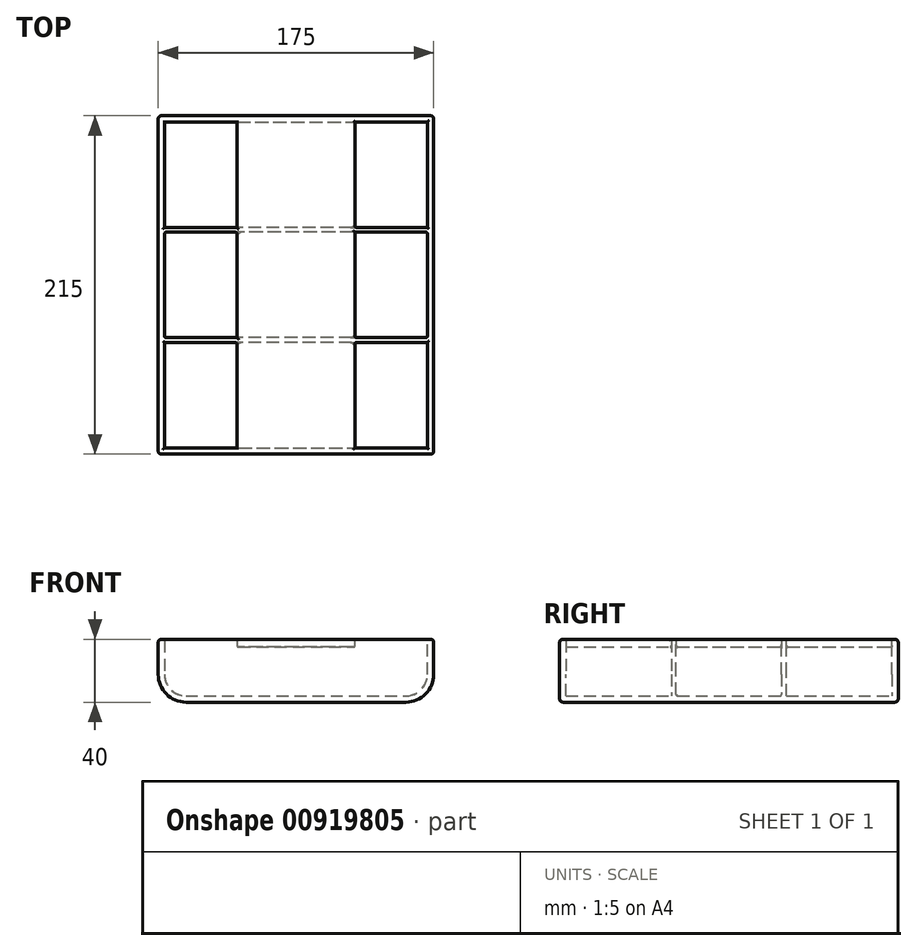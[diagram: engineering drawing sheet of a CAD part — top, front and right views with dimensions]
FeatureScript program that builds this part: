
annotation { "Feature Type Name" : "Feature", "Feature Type Description" : "" }
export const myFeature = defineFeature(function(context is Context, id is Id, definition is map)
    precondition{}
    {
        {
            var Q0;
            Q0=qCreatedBy(makeId("Front.planeOp"),FACE);
            var sketch = newSketch(context, id + "F0", { "sketchPlane" : qUnion([Q0])});
            skLineSegment(sketch, "E0", {"start": v(-91.07, 3.96) * mm, "end": v(-87.07, 3.96) * mm});
            skLineSegment(sketch, "E1", {"start": v(-87.07, 3.96) * mm, "end": v(-87.07, -18.39) * mm});
            skLineSegment(sketch, "E2", {"start": v(-73.42, -32.04) * mm, "end": v(66.28, -32.04) * mm});
            skLineSegment(sketch, "E3", {"start": v(79.93, -18.39) * mm, "end": v(79.93, 3.96) * mm});
            skLineSegment(sketch, "E4", {"start": v(79.93, 3.96) * mm, "end": v(83.93, 3.96) * mm});
            skLineSegment(sketch, "E5", {"start": v(83.93, 3.96) * mm, "end": v(83.93, -18.39) * mm});
            skLineSegment(sketch, "E6", {"start": v(66.28, -36.04) * mm, "end": v(-73.42, -36.04) * mm});
            skLineSegment(sketch, "E7", {"start": v(-91.07, -18.39) * mm, "end": v(-91.07, 3.96) * mm});
            skArc(sketch, "E8", {"start": v(-91.07, -18.39) * mm, "mid": v(-85.9, -30.87) * mm, "end": v(-73.42, -36.04) * mm});
            skArc(sketch, "E9", {"start": v(-87.07, -18.39) * mm, "mid": v(-83.07, -28.04) * mm, "end": v(-73.42, -32.04) * mm});
            skArc(sketch, "E10", {"start": v(66.28, -32.04) * mm, "mid": v(75.93, -28.04) * mm, "end": v(79.93, -18.39) * mm});
            skArc(sketch, "E11", {"start": v(66.28, -36.04) * mm, "mid": v(78.76, -30.87) * mm, "end": v(83.93, -18.39) * mm});
            skSolve(sketch);
        }
        {
            var Q0;
            Q0 = qSketchRegion(id + "F0", true);
            extrude(context, id + "F1", {"entities" : qUnion([Q0]), "depth" : (67 * 3 + 6) * mm, "offsetDistance" : 25 * mm});
        }
        {
            var Q0;
            Q0=makeQuery(id+"F1.opExtrude","CAP_FACE",FACE,{"disambiguationData":[OSD([sQuery(id+"F0.wireOp",EDGE,"E0"),sQuery(id+"F0.wireOp",EDGE,"E1"),sQuery(id+"F0.wireOp",EDGE,"E2"),sQuery(id+"F0.wireOp",EDGE,"E3"),sQuery(id+"F0.wireOp",EDGE,"E4"),sQuery(id+"F0.wireOp",EDGE,"E5"),sQuery(id+"F0.wireOp",EDGE,"E6"),sQuery(id+"F0.wireOp",EDGE,"E7"),sQuery(id+"F0.wireOp",EDGE,"E8"),sQuery(id+"F0.wireOp",EDGE,"E9"),sQuery(id+"F0.wireOp",EDGE,"E10"),sQuery(id+"F0.wireOp",EDGE,"E11")])],"isStart":false});
            var sketch = newSketch(context, id + "F2", { "sketchPlane" : qUnion([Q0])});
            skLineSegment(sketch, "E12", {"start": v(-91.07, 3.96) * mm, "end": v(-91.07, -18.39) * mm});
            skLineSegment(sketch, "E13", {"start": v(-91.07, 3.96) * mm, "end": v(83.93, 3.96) * mm});
            skLineSegment(sketch, "E14", {"start": v(83.93, 3.96) * mm, "end": v(83.93, -18.39) * mm});
            skLineSegment(sketch, "E15", {"start": v(66.28, -36.04) * mm, "end": v(-73.42, -36.04) * mm});
            skArc(sketch, "E16", {"start": v(-91.07, -18.39) * mm, "mid": v(-85.9, -30.87) * mm, "end": v(-73.42, -36.04) * mm});
            skArc(sketch, "E17", {"start": v(66.28, -36.04) * mm, "mid": v(78.76, -30.87) * mm, "end": v(83.93, -18.39) * mm});
            skSolve(sketch);
        }
        {
            var Q0;
            Q0 = qSketchRegion(id + "F2", true);
            extrude(context, id + "F3", {"entities" : qUnion([Q0]), "operationType" : NewBodyOperationType.ADD, "depth" : 4 * mm, "offsetDistance" : 25 * mm});
        }
        {
            var Q0;
            Q0=makeQuery(id+"F1.opExtrude","CAP_FACE",FACE,{"disambiguationData":[OSD([sQuery(id+"F0.wireOp",EDGE,"E0"),sQuery(id+"F0.wireOp",EDGE,"E1"),sQuery(id+"F0.wireOp",EDGE,"E2"),sQuery(id+"F0.wireOp",EDGE,"E3"),sQuery(id+"F0.wireOp",EDGE,"E4"),sQuery(id+"F0.wireOp",EDGE,"E5"),sQuery(id+"F0.wireOp",EDGE,"E6"),sQuery(id+"F0.wireOp",EDGE,"E7"),sQuery(id+"F0.wireOp",EDGE,"E8"),sQuery(id+"F0.wireOp",EDGE,"E9"),sQuery(id+"F0.wireOp",EDGE,"E10"),sQuery(id+"F0.wireOp",EDGE,"E11")])],"isStart":true});
            var sketch = newSketch(context, id + "F4", { "sketchPlane" : qUnion([Q0])});
            skLineSegment(sketch, "E18", {"start": v(-83.93, -18.39) * mm, "end": v(-83.93, 3.96) * mm});
            skLineSegment(sketch, "E19", {"start": v(-83.93, 3.96) * mm, "end": v(91.07, 3.96) * mm});
            skLineSegment(sketch, "E20", {"start": v(91.07, 3.96) * mm, "end": v(91.07, -18.39) * mm});
            skLineSegment(sketch, "E21", {"start": v(73.42, -36.04) * mm, "end": v(-66.28, -36.04) * mm});
            skArc(sketch, "E22", {"start": v(-83.93, -18.39) * mm, "mid": v(-78.76, -30.87) * mm, "end": v(-66.28, -36.04) * mm});
            skArc(sketch, "E23", {"start": v(73.42, -36.04) * mm, "mid": v(85.9, -30.87) * mm, "end": v(91.07, -18.39) * mm});
            skSolve(sketch);
        }
        {
            var Q0;
            Q0 = qSketchRegion(id + "F4", true);
            extrude(context, id + "F5", {"entities" : qUnion([Q0]), "operationType" : NewBodyOperationType.ADD, "depth" : 4 * mm, "offsetDistance" : 25 * mm});
        }
        {
            var Q0;
            Q0=qCreatedBy(makeId("Front.planeOp"),FACE);
            cPlane(context, id + "F6", {"entities" : qUnion([Q0]), "cplaneType" : CPlaneType.OFFSET, "offset" : 67 * mm, "width" : 150 * mm, "height" : 150 * mm});
        }
        {
            var Q0;
            Q0=qCreatedBy(makeId("Front.planeOp"),FACE);
            cPlane(context, id + "F7", {"entities" : qUnion([Q0]), "cplaneType" : CPlaneType.OFFSET, "offset" : (67 * 2 + 3) * mm, "width" : 150 * mm, "height" : 150 * mm});
        }
        {
            var Q0;
            Q0=qCreatedBy(id+"F6.planeOp",FACE);
            var sketch = newSketch(context, id + "F8", { "sketchPlane" : qUnion([Q0])});
            skLineSegment(sketch, "E24", {"start": v(-87.07, -18.39) * mm, "end": v(-87.07, 3.96) * mm});
            skLineSegment(sketch, "E25", {"start": v(-87.07, 3.96) * mm, "end": v(79.93, 3.96) * mm});
            skLineSegment(sketch, "E26", {"start": v(79.93, 3.96) * mm, "end": v(79.93, -18.39) * mm});
            skLineSegment(sketch, "E27", {"start": v(66.28, -32.04) * mm, "end": v(-73.42, -32.04) * mm});
            skArc(sketch, "E28", {"start": v(-87.07, -18.39) * mm, "mid": v(-83.07, -28.04) * mm, "end": v(-73.42, -32.04) * mm});
            skArc(sketch, "E29", {"start": v(66.28, -32.04) * mm, "mid": v(75.93, -28.04) * mm, "end": v(79.93, -18.39) * mm});
            skSolve(sketch);
        }
        {
            var Q0;
            Q0 = qSketchRegion(id + "F8", true);
            extrude(context, id + "F9", {"entities" : qUnion([Q0]), "operationType" : NewBodyOperationType.ADD, "depth" : 3 * mm, "offsetDistance" : 25 * mm});
        }
        {
            var Q0;
            Q0=qCreatedBy(id+"F7.planeOp",FACE);
            var sketch = newSketch(context, id + "F10", { "sketchPlane" : qUnion([Q0])});
            skLineSegment(sketch, "E30", {"start": v(-87.06, -18.13) * mm, "end": v(-87.06, 3.96) * mm});
            skLineSegment(sketch, "E31", {"start": v(-87.06, 3.96) * mm, "end": v(79.93, 3.96) * mm});
            skLineSegment(sketch, "E32", {"start": v(79.93, 3.96) * mm, "end": v(79.93, -18.02) * mm});
            skLineSegment(sketch, "E33", {"start": v(66.28, -32.04) * mm, "end": v(-73.42, -32.04) * mm});
            skArc(sketch, "E34", {"start": v(-87.06, -18.13) * mm, "mid": v(-83.16, -27.95) * mm, "end": v(-73.42, -32.04) * mm});
            skArc(sketch, "E35", {"start": v(66.28, -32.04) * mm, "mid": v(76.06, -27.9) * mm, "end": v(79.93, -18.02) * mm});
            skSolve(sketch);
        }
        {
            var Q0;
            Q0 = qSketchRegion(id + "F10", true);
            extrude(context, id + "F11", {"entities" : qUnion([Q0]), "operationType" : NewBodyOperationType.ADD, "depth" : 3 * mm, "offsetDistance" : 25 * mm});
        }
        {
            var Q0;
            Q0=makeQuery(id+"F5.opExtrude","CAP_FACE",FACE,{"disambiguationData":[OSD([sQuery(id+"F4.wireOp",EDGE,"E18"),sQuery(id+"F4.wireOp",EDGE,"E19"),sQuery(id+"F4.wireOp",EDGE,"E20"),sQuery(id+"F4.wireOp",EDGE,"E21"),sQuery(id+"F4.wireOp",EDGE,"E22"),sQuery(id+"F4.wireOp",EDGE,"E23")])],"isStart":true});
            var sketch = newSketch(context, id + "F12", { "sketchPlane" : qUnion([Q0])});
            skLineSegment(sketch, "E36", {"start": v(-41.07, 3.96) * mm, "end": v(-41.07, -1.04) * mm});
            skLineSegment(sketch, "E37", {"start": v(-41.07, -1.04) * mm, "end": v(33.93, -1.04) * mm});
            skLineSegment(sketch, "E38", {"start": v(33.93, -1.04) * mm, "end": v(33.93, 3.96) * mm});
            skLineSegment(sketch, "E39", {"start": v(33.93, 3.96) * mm, "end": v(-41.07, 3.96) * mm});
            skSolve(sketch);
        }
        {
            var Q0;
            Q0 = qSketchRegion(id + "F12", true);
            extrude(context, id + "F13", {"entities" : qUnion([Q0]), "operationType" : NewBodyOperationType.ADD, "depth" : 207 * mm, "offsetDistance" : 25 * mm});
        }
        {
            var Q0;
            {var subQ0=sQuery(id+"F12.wireOp",EDGE,"E37");var subQ1=sQuery(id+"F12.wireOp",EDGE,"E38");Q0=makeQuery(id+"F13.boolean.opBoolean","SPLIT",EDGE,{"disambiguationData":[TD([makeQuery(id+"F3.opExtrude","CAP_FACE",FACE,{"disambiguationData":[OSD([sQuery(id+"F2.wireOp",EDGE,"E12"),sQuery(id+"F2.wireOp",EDGE,"E13"),sQuery(id+"F2.wireOp",EDGE,"E14"),sQuery(id+"F2.wireOp",EDGE,"E15"),sQuery(id+"F2.wireOp",EDGE,"E16"),sQuery(id+"F2.wireOp",EDGE,"E17")])],"isStart":true})])],"derivedFrom":makeQuery(id+"F13.opExtrude","SWEPT_EDGE",EDGE,{"disambiguationData":[OSD([subQ0,subQ1])]})});}
            var Q1;
            {var subQ0=sQuery(id+"F2.wireOp",EDGE,"E13");var subQ2=sQuery(id+"F12.wireOp",EDGE,"E38");var subQ3=sQuery(id+"F4.wireOp",EDGE,"E19");var subQ4=sQuery(id+"F12.wireOp",EDGE,"E39");Q1=makeQuery(id+"F13.boolean.opBoolean","SPLIT",EDGE,{"disambiguationData":[TD([makeQuery(id+"F3.opExtrude","CAP_FACE",FACE,{"disambiguationData":[OSD([sQuery(id+"F2.wireOp",EDGE,"E12"),subQ0,sQuery(id+"F2.wireOp",EDGE,"E14"),sQuery(id+"F2.wireOp",EDGE,"E15"),sQuery(id+"F2.wireOp",EDGE,"E16"),sQuery(id+"F2.wireOp",EDGE,"E17")])],"isStart":true})])],"derivedFrom":makeQuery(id+"F13.opExtrude","SWEPT_EDGE",EDGE,{"disambiguationData":[OSD([subQ3,subQ2,subQ4])]})});}
            var Q2;
            {var subQ0=sQuery(id+"F10.wireOp",EDGE,"E31");Q2=makeQuery(id+"F13.boolean.opBoolean","SPLIT",EDGE,{"disambiguationData":[TD([makeQuery(id+"F1.opExtrude","SWEPT_FACE",FACE,{"disambiguationData":[OSD([sQuery(id+"F0.wireOp",EDGE,"E3")])]})])],"derivedFrom":makeQuery(id+"F11.opExtrude","CAP_EDGE",EDGE,{"disambiguationData":[OSD([subQ0])],"isStart":false})});}
            var Q3;
            {var subQ0=sQuery(id+"F10.wireOp",EDGE,"E31");Q3=makeQuery(id+"F13.boolean.opBoolean","SPLIT",EDGE,{"disambiguationData":[TD([makeQuery(id+"F1.opExtrude","SWEPT_FACE",FACE,{"disambiguationData":[OSD([sQuery(id+"F0.wireOp",EDGE,"E3")])]})])],"derivedFrom":makeQuery(id+"F11.opExtrude","CAP_EDGE",EDGE,{"disambiguationData":[OSD([subQ0])],"isStart":true})});}
            var Q4;
            {var subQ0=sQuery(id+"F12.wireOp",EDGE,"E38");var subQ1=sQuery(id+"F12.wireOp",EDGE,"E37");Q4=makeQuery(id+"F13.boolean.opBoolean","SPLIT",EDGE,{"disambiguationData":[TD([makeQuery(id+"F9.opExtrude","CAP_FACE",FACE,{"disambiguationData":[OSD([sQuery(id+"F8.wireOp",EDGE,"E24"),sQuery(id+"F8.wireOp",EDGE,"E25"),sQuery(id+"F8.wireOp",EDGE,"E26"),sQuery(id+"F8.wireOp",EDGE,"E27"),sQuery(id+"F8.wireOp",EDGE,"E28"),sQuery(id+"F8.wireOp",EDGE,"E29")])],"isStart":false})])],"derivedFrom":makeQuery(id+"F13.opExtrude","SWEPT_EDGE",EDGE,{"disambiguationData":[OSD([subQ1,subQ0])]})});}
            var Q5;
            {var subQ0=sQuery(id+"F4.wireOp",EDGE,"E19");var subQ1=sQuery(id+"F8.wireOp",EDGE,"E25");var subQ2=sQuery(id+"F12.wireOp",EDGE,"E38");var subQ4=sQuery(id+"F12.wireOp",EDGE,"E39");Q5=makeQuery(id+"F13.boolean.opBoolean","SPLIT",EDGE,{"disambiguationData":[TD([makeQuery(id+"F9.opExtrude","CAP_FACE",FACE,{"disambiguationData":[OSD([sQuery(id+"F8.wireOp",EDGE,"E24"),subQ1,sQuery(id+"F8.wireOp",EDGE,"E26"),sQuery(id+"F8.wireOp",EDGE,"E27"),sQuery(id+"F8.wireOp",EDGE,"E28"),sQuery(id+"F8.wireOp",EDGE,"E29")])],"isStart":false})])],"derivedFrom":makeQuery(id+"F13.opExtrude","SWEPT_EDGE",EDGE,{"disambiguationData":[OSD([subQ0,subQ2,subQ4])]})});}
            var Q6;
            {var subQ0=sQuery(id+"F2.wireOp",EDGE,"E13");var subQ1=makeQuery(id+"F3.opExtrude","CAP_FACE",FACE,{"disambiguationData":[OSD([sQuery(id+"F2.wireOp",EDGE,"E12"),subQ0,sQuery(id+"F2.wireOp",EDGE,"E14"),sQuery(id+"F2.wireOp",EDGE,"E15"),sQuery(id+"F2.wireOp",EDGE,"E16"),sQuery(id+"F2.wireOp",EDGE,"E17")])],"isStart":true});var subQ2=sQuery(id+"F0.wireOp",EDGE,"E4");var subQ4=sQuery(id+"F0.wireOp",EDGE,"E3");Q6=makeQuery(id+"F11.boolean.opBoolean","SPLIT",EDGE,{"disambiguationData":[TD([subQ1])],"derivedFrom":makeQuery(id+"F9.boolean.opBoolean","SPLIT",EDGE,{"disambiguationData":[TD([subQ1])],"derivedFrom":makeQuery(id+"F1.opExtrude","SWEPT_EDGE",EDGE,{"disambiguationData":[OSD([subQ4,subQ2])]})})});}
            var Q7;
            {var subQ0=sQuery(id+"F2.wireOp",EDGE,"E13");Q7=makeQuery(id+"F13.boolean.opBoolean","SPLIT",EDGE,{"disambiguationData":[TD([makeQuery(id+"F1.opExtrude","SWEPT_FACE",FACE,{"disambiguationData":[OSD([sQuery(id+"F0.wireOp",EDGE,"E3")])]})])],"derivedFrom":makeQuery(id+"F3.opExtrude","CAP_EDGE",EDGE,{"disambiguationData":[OSD([subQ0])],"isStart":true})});}
            var Q8;
            {var subQ0=sQuery(id+"F12.wireOp",EDGE,"E37");var subQ1=sQuery(id+"F12.wireOp",EDGE,"E36");Q8=makeQuery(id+"F13.boolean.opBoolean","SPLIT",EDGE,{"disambiguationData":[TD([makeQuery(id+"F3.opExtrude","CAP_FACE",FACE,{"disambiguationData":[OSD([sQuery(id+"F2.wireOp",EDGE,"E12"),sQuery(id+"F2.wireOp",EDGE,"E13"),sQuery(id+"F2.wireOp",EDGE,"E14"),sQuery(id+"F2.wireOp",EDGE,"E15"),sQuery(id+"F2.wireOp",EDGE,"E16"),sQuery(id+"F2.wireOp",EDGE,"E17")])],"isStart":true})])],"derivedFrom":makeQuery(id+"F13.opExtrude","SWEPT_EDGE",EDGE,{"disambiguationData":[OSD([subQ1,subQ0])]})});}
            var Q9;
            {var subQ0=sQuery(id+"F2.wireOp",EDGE,"E13");Q9=makeQuery(id+"F13.boolean.opBoolean","SPLIT",EDGE,{"disambiguationData":[TD([makeQuery(id+"F1.opExtrude","SWEPT_FACE",FACE,{"disambiguationData":[OSD([sQuery(id+"F0.wireOp",EDGE,"E1")])]})])],"derivedFrom":makeQuery(id+"F3.opExtrude","CAP_EDGE",EDGE,{"disambiguationData":[OSD([subQ0])],"isStart":true})});}
            var Q10;
            {var subQ0=sQuery(id+"F2.wireOp",EDGE,"E13");var subQ1=makeQuery(id+"F3.opExtrude","CAP_FACE",FACE,{"disambiguationData":[OSD([sQuery(id+"F2.wireOp",EDGE,"E12"),subQ0,sQuery(id+"F2.wireOp",EDGE,"E14"),sQuery(id+"F2.wireOp",EDGE,"E15"),sQuery(id+"F2.wireOp",EDGE,"E16"),sQuery(id+"F2.wireOp",EDGE,"E17")])],"isStart":true});var subQ3=sQuery(id+"F0.wireOp",EDGE,"E1");var subQ5=sQuery(id+"F0.wireOp",EDGE,"E0");Q10=makeQuery(id+"F11.boolean.opBoolean","SPLIT",EDGE,{"disambiguationData":[TD([subQ1])],"derivedFrom":makeQuery(id+"F9.boolean.opBoolean","SPLIT",EDGE,{"disambiguationData":[TD([subQ1])],"derivedFrom":makeQuery(id+"F1.opExtrude","SWEPT_EDGE",EDGE,{"disambiguationData":[OSD([subQ5,subQ3])]})})});}
            var Q11;
            {var subQ0=sQuery(id+"F10.wireOp",EDGE,"E31");Q11=makeQuery(id+"F13.boolean.opBoolean","SPLIT",EDGE,{"disambiguationData":[TD([makeQuery(id+"F1.opExtrude","SWEPT_FACE",FACE,{"disambiguationData":[OSD([sQuery(id+"F0.wireOp",EDGE,"E1")])]})])],"derivedFrom":makeQuery(id+"F11.opExtrude","CAP_EDGE",EDGE,{"disambiguationData":[OSD([subQ0])],"isStart":false})});}
            var Q12;
            {var subQ0=sQuery(id+"F10.wireOp",EDGE,"E31");Q12=makeQuery(id+"F13.boolean.opBoolean","SPLIT",EDGE,{"disambiguationData":[TD([makeQuery(id+"F1.opExtrude","SWEPT_FACE",FACE,{"disambiguationData":[OSD([sQuery(id+"F0.wireOp",EDGE,"E1")])]})])],"derivedFrom":makeQuery(id+"F11.opExtrude","CAP_EDGE",EDGE,{"disambiguationData":[OSD([subQ0])],"isStart":true})});}
            var Q13;
            {var subQ0=sQuery(id+"F12.wireOp",EDGE,"E36");var subQ1=sQuery(id+"F12.wireOp",EDGE,"E37");Q13=makeQuery(id+"F13.boolean.opBoolean","SPLIT",EDGE,{"disambiguationData":[TD([makeQuery(id+"F9.opExtrude","CAP_FACE",FACE,{"disambiguationData":[OSD([sQuery(id+"F8.wireOp",EDGE,"E24"),sQuery(id+"F8.wireOp",EDGE,"E25"),sQuery(id+"F8.wireOp",EDGE,"E26"),sQuery(id+"F8.wireOp",EDGE,"E27"),sQuery(id+"F8.wireOp",EDGE,"E28"),sQuery(id+"F8.wireOp",EDGE,"E29")])],"isStart":false})])],"derivedFrom":makeQuery(id+"F13.opExtrude","SWEPT_EDGE",EDGE,{"disambiguationData":[OSD([subQ0,subQ1])]})});}
            var Q14;
            {var subQ0=sQuery(id+"F4.wireOp",EDGE,"E19");var subQ1=sQuery(id+"F8.wireOp",EDGE,"E25");var subQ3=sQuery(id+"F12.wireOp",EDGE,"E36");var subQ4=sQuery(id+"F12.wireOp",EDGE,"E39");Q14=makeQuery(id+"F13.boolean.opBoolean","SPLIT",EDGE,{"disambiguationData":[TD([makeQuery(id+"F9.opExtrude","CAP_FACE",FACE,{"disambiguationData":[OSD([sQuery(id+"F8.wireOp",EDGE,"E24"),subQ1,sQuery(id+"F8.wireOp",EDGE,"E26"),sQuery(id+"F8.wireOp",EDGE,"E27"),sQuery(id+"F8.wireOp",EDGE,"E28"),sQuery(id+"F8.wireOp",EDGE,"E29")])],"isStart":false})])],"derivedFrom":makeQuery(id+"F13.opExtrude","SWEPT_EDGE",EDGE,{"disambiguationData":[OSD([subQ0,subQ3,subQ4])]})});}
            var Q15;
            {var subQ0=sQuery(id+"F8.wireOp",EDGE,"E25");Q15=makeQuery(id+"F13.boolean.opBoolean","SPLIT",EDGE,{"disambiguationData":[TD([makeQuery(id+"F1.opExtrude","SWEPT_FACE",FACE,{"disambiguationData":[OSD([sQuery(id+"F0.wireOp",EDGE,"E3")])]})])],"derivedFrom":makeQuery(id+"F9.opExtrude","CAP_EDGE",EDGE,{"disambiguationData":[OSD([subQ0])],"isStart":false})});}
            var Q16;
            {var subQ0=sQuery(id+"F2.wireOp",EDGE,"E13");var subQ2=sQuery(id+"F0.wireOp",EDGE,"E4");var subQ4=sQuery(id+"F0.wireOp",EDGE,"E3");var subQ8=sQuery(id+"F8.wireOp",EDGE,"E25");var subQ11=makeQuery(id+"F9.opExtrude","CAP_FACE",FACE,{"disambiguationData":[OSD([sQuery(id+"F8.wireOp",EDGE,"E24"),subQ8,sQuery(id+"F8.wireOp",EDGE,"E26"),sQuery(id+"F8.wireOp",EDGE,"E27"),sQuery(id+"F8.wireOp",EDGE,"E28"),sQuery(id+"F8.wireOp",EDGE,"E29")])],"isStart":false});Q16=makeQuery(id+"F11.boolean.opBoolean","SPLIT",EDGE,{"disambiguationData":[TD([subQ11])],"derivedFrom":makeQuery(id+"F9.boolean.opBoolean","SPLIT",EDGE,{"disambiguationData":[TD([makeQuery(id+"F3.opExtrude","CAP_FACE",FACE,{"disambiguationData":[OSD([sQuery(id+"F2.wireOp",EDGE,"E12"),subQ0,sQuery(id+"F2.wireOp",EDGE,"E14"),sQuery(id+"F2.wireOp",EDGE,"E15"),sQuery(id+"F2.wireOp",EDGE,"E16"),sQuery(id+"F2.wireOp",EDGE,"E17")])],"isStart":true})])],"derivedFrom":makeQuery(id+"F1.opExtrude","SWEPT_EDGE",EDGE,{"disambiguationData":[OSD([subQ4,subQ2])]})})});}
            var Q17;
            {var subQ0=sQuery(id+"F2.wireOp",EDGE,"E13");var subQ3=sQuery(id+"F0.wireOp",EDGE,"E1");var subQ6=sQuery(id+"F0.wireOp",EDGE,"E0");var subQ8=sQuery(id+"F8.wireOp",EDGE,"E25");var subQ11=makeQuery(id+"F9.opExtrude","CAP_FACE",FACE,{"disambiguationData":[OSD([sQuery(id+"F8.wireOp",EDGE,"E24"),subQ8,sQuery(id+"F8.wireOp",EDGE,"E26"),sQuery(id+"F8.wireOp",EDGE,"E27"),sQuery(id+"F8.wireOp",EDGE,"E28"),sQuery(id+"F8.wireOp",EDGE,"E29")])],"isStart":false});Q17=makeQuery(id+"F11.boolean.opBoolean","SPLIT",EDGE,{"disambiguationData":[TD([subQ11])],"derivedFrom":makeQuery(id+"F9.boolean.opBoolean","SPLIT",EDGE,{"disambiguationData":[TD([makeQuery(id+"F3.opExtrude","CAP_FACE",FACE,{"disambiguationData":[OSD([sQuery(id+"F2.wireOp",EDGE,"E12"),subQ0,sQuery(id+"F2.wireOp",EDGE,"E14"),sQuery(id+"F2.wireOp",EDGE,"E15"),sQuery(id+"F2.wireOp",EDGE,"E16"),sQuery(id+"F2.wireOp",EDGE,"E17")])],"isStart":true})])],"derivedFrom":makeQuery(id+"F1.opExtrude","SWEPT_EDGE",EDGE,{"disambiguationData":[OSD([subQ6,subQ3])]})})});}
            var Q18;
            {var subQ0=sQuery(id+"F8.wireOp",EDGE,"E25");Q18=makeQuery(id+"F13.boolean.opBoolean","SPLIT",EDGE,{"disambiguationData":[TD([makeQuery(id+"F1.opExtrude","SWEPT_FACE",FACE,{"disambiguationData":[OSD([sQuery(id+"F0.wireOp",EDGE,"E1")])]})])],"derivedFrom":makeQuery(id+"F9.opExtrude","CAP_EDGE",EDGE,{"disambiguationData":[OSD([subQ0])],"isStart":false})});}
            var Q19;
            {var subQ0=sQuery(id+"F8.wireOp",EDGE,"E25");Q19=makeQuery(id+"F13.boolean.opBoolean","SPLIT",EDGE,{"disambiguationData":[TD([makeQuery(id+"F1.opExtrude","SWEPT_FACE",FACE,{"disambiguationData":[OSD([sQuery(id+"F0.wireOp",EDGE,"E1")])]})])],"derivedFrom":makeQuery(id+"F9.opExtrude","CAP_EDGE",EDGE,{"disambiguationData":[OSD([subQ0])],"isStart":true})});}
            var Q20;
            {var subQ0=sQuery(id+"F12.wireOp",EDGE,"E37");var subQ1=sQuery(id+"F12.wireOp",EDGE,"E36");Q20=makeQuery(id+"F13.boolean.opBoolean","SPLIT",EDGE,{"disambiguationData":[TD([makeQuery(id+"F5.opExtrude","CAP_FACE",FACE,{"disambiguationData":[OSD([sQuery(id+"F4.wireOp",EDGE,"E18"),sQuery(id+"F4.wireOp",EDGE,"E19"),sQuery(id+"F4.wireOp",EDGE,"E20"),sQuery(id+"F4.wireOp",EDGE,"E21"),sQuery(id+"F4.wireOp",EDGE,"E22"),sQuery(id+"F4.wireOp",EDGE,"E23")])],"isStart":true})])],"derivedFrom":makeQuery(id+"F13.opExtrude","SWEPT_EDGE",EDGE,{"disambiguationData":[OSD([subQ1,subQ0])]})});}
            var Q21;
            {var subQ0=sQuery(id+"F4.wireOp",EDGE,"E19");var subQ1=sQuery(id+"F12.wireOp",EDGE,"E36");var subQ3=sQuery(id+"F12.wireOp",EDGE,"E39");Q21=makeQuery(id+"F13.boolean.opBoolean","SPLIT",EDGE,{"disambiguationData":[TD([makeQuery(id+"F5.opExtrude","CAP_FACE",FACE,{"disambiguationData":[OSD([sQuery(id+"F4.wireOp",EDGE,"E18"),subQ0,sQuery(id+"F4.wireOp",EDGE,"E20"),sQuery(id+"F4.wireOp",EDGE,"E21"),sQuery(id+"F4.wireOp",EDGE,"E22"),sQuery(id+"F4.wireOp",EDGE,"E23")])],"isStart":true})])],"derivedFrom":makeQuery(id+"F13.opExtrude","SWEPT_EDGE",EDGE,{"disambiguationData":[OSD([subQ0,subQ1,subQ3])]})});}
            var Q22;
            {var subQ0=sQuery(id+"F0.wireOp",EDGE,"E1");var subQ1=sQuery(id+"F0.wireOp",EDGE,"E0");var subQ3=sQuery(id+"F4.wireOp",EDGE,"E19");Q22=makeQuery(id+"F9.boolean.opBoolean","SPLIT",EDGE,{"disambiguationData":[TD([makeQuery(id+"F5.opExtrude","CAP_FACE",FACE,{"disambiguationData":[OSD([sQuery(id+"F4.wireOp",EDGE,"E18"),subQ3,sQuery(id+"F4.wireOp",EDGE,"E20"),sQuery(id+"F4.wireOp",EDGE,"E21"),sQuery(id+"F4.wireOp",EDGE,"E22"),sQuery(id+"F4.wireOp",EDGE,"E23")])],"isStart":true})])],"derivedFrom":makeQuery(id+"F1.opExtrude","SWEPT_EDGE",EDGE,{"disambiguationData":[OSD([subQ1,subQ0])]})});}
            var Q23;
            Q23=makeQuery(id+"F13.boolean.opBoolean","INTERSECT",EDGE,{"derivedFrom":[makeQuery(id+"F9.opExtrude","CAP_FACE",FACE,{"disambiguationData":[OSD([sQuery(id+"F8.wireOp",EDGE,"E24"),sQuery(id+"F8.wireOp",EDGE,"E25"),sQuery(id+"F8.wireOp",EDGE,"E26"),sQuery(id+"F8.wireOp",EDGE,"E27"),sQuery(id+"F8.wireOp",EDGE,"E28"),sQuery(id+"F8.wireOp",EDGE,"E29")])],"isStart":false}),makeQuery(id+"F13.opExtrude","SWEPT_FACE",FACE,{"disambiguationData":[OSD([sQuery(id+"F12.wireOp",EDGE,"E36")])]})]});
            var Q24;
            Q24=makeQuery(id+"F13.boolean.opBoolean","INTERSECT",EDGE,{"derivedFrom":[makeQuery(id+"F11.opExtrude","CAP_FACE",FACE,{"disambiguationData":[OSD([sQuery(id+"F10.wireOp",EDGE,"E30"),sQuery(id+"F10.wireOp",EDGE,"E31"),sQuery(id+"F10.wireOp",EDGE,"E32"),sQuery(id+"F10.wireOp",EDGE,"E33"),sQuery(id+"F10.wireOp",EDGE,"E34"),sQuery(id+"F10.wireOp",EDGE,"E35")])],"isStart":false}),makeQuery(id+"F13.opExtrude","SWEPT_FACE",FACE,{"disambiguationData":[OSD([sQuery(id+"F12.wireOp",EDGE,"E36")])]})]});
            var Q25;
            {var subQ0=sQuery(id+"F0.wireOp",EDGE,"E2");var subQ1=sQuery(id+"F0.wireOp",EDGE,"E10");Q25=makeQuery(id+"F9.boolean.opBoolean","SPLIT",EDGE,{"disambiguationData":[TD([makeQuery(id+"F5.opExtrude","CAP_FACE",FACE,{"disambiguationData":[OSD([sQuery(id+"F4.wireOp",EDGE,"E18"),sQuery(id+"F4.wireOp",EDGE,"E19"),sQuery(id+"F4.wireOp",EDGE,"E20"),sQuery(id+"F4.wireOp",EDGE,"E21"),sQuery(id+"F4.wireOp",EDGE,"E22"),sQuery(id+"F4.wireOp",EDGE,"E23")])],"isStart":true})])],"derivedFrom":makeQuery(id+"F1.opExtrude","SWEPT_EDGE",EDGE,{"disambiguationData":[OSD([subQ0,subQ1])]})});}
            var Q26;
            Q26=makeQuery(id+"F5.boolean.opBoolean","MERGE",EDGE,{"derivedFrom":[makeQuery(id+"F3.boolean.opBoolean","MERGE",EDGE,{"derivedFrom":[makeQuery(id+"F1.opExtrude","SWEPT_EDGE",EDGE,{"disambiguationData":[OSD([sQuery(id+"F0.wireOp",EDGE,"E6"),sQuery(id+"F0.wireOp",EDGE,"E11")])]}),makeQuery(id+"F3.opExtrude","SWEPT_EDGE",EDGE,{"disambiguationData":[OSD([sQuery(id+"F2.wireOp",EDGE,"E15"),sQuery(id+"F2.wireOp",EDGE,"E17")])]})]}),makeQuery(id+"F5.opExtrude","SWEPT_EDGE",EDGE,{"disambiguationData":[OSD([sQuery(id+"F4.wireOp",EDGE,"E21"),sQuery(id+"F4.wireOp",EDGE,"E22")])]})]});
            var Q27;
            Q27=makeQuery(id+"F13.boolean.opBoolean","INTERSECT",EDGE,{"derivedFrom":[makeQuery(id+"F11.opExtrude","CAP_FACE",FACE,{"disambiguationData":[OSD([sQuery(id+"F10.wireOp",EDGE,"E30"),sQuery(id+"F10.wireOp",EDGE,"E31"),sQuery(id+"F10.wireOp",EDGE,"E32"),sQuery(id+"F10.wireOp",EDGE,"E33"),sQuery(id+"F10.wireOp",EDGE,"E34"),sQuery(id+"F10.wireOp",EDGE,"E35")])],"isStart":false}),makeQuery(id+"F13.opExtrude","SWEPT_FACE",FACE,{"disambiguationData":[OSD([sQuery(id+"F12.wireOp",EDGE,"E38")])]})]});
            var Q28;
            Q28=makeQuery(id+"F13.opExtrude","CAP_EDGE",EDGE,{"disambiguationData":[OSD([sQuery(id+"F12.wireOp",EDGE,"E38")])],"isStart":false});
            var Q29;
            Q29=makeQuery(id+"F13.boolean.opBoolean","INTERSECT",EDGE,{"derivedFrom":[makeQuery(id+"F11.opExtrude","CAP_FACE",FACE,{"disambiguationData":[OSD([sQuery(id+"F10.wireOp",EDGE,"E30"),sQuery(id+"F10.wireOp",EDGE,"E31"),sQuery(id+"F10.wireOp",EDGE,"E32"),sQuery(id+"F10.wireOp",EDGE,"E33"),sQuery(id+"F10.wireOp",EDGE,"E34"),sQuery(id+"F10.wireOp",EDGE,"E35")])],"isStart":true}),makeQuery(id+"F13.opExtrude","SWEPT_FACE",FACE,{"disambiguationData":[OSD([sQuery(id+"F12.wireOp",EDGE,"E38")])]})]});
            var Q30;
            {var subQ0=sQuery(id+"F4.wireOp",EDGE,"E19");Q30=makeQuery(id+"F13.boolean.opBoolean","SPLIT",EDGE,{"disambiguationData":[TD([makeQuery(id+"F1.opExtrude","SWEPT_FACE",FACE,{"disambiguationData":[OSD([sQuery(id+"F0.wireOp",EDGE,"E3")])]})])],"derivedFrom":makeQuery(id+"F5.opExtrude","CAP_EDGE",EDGE,{"disambiguationData":[OSD([subQ0])],"isStart":true})});}
            var Q31;
            {var subQ0=sQuery(id+"F4.wireOp",EDGE,"E19");var subQ2=sQuery(id+"F12.wireOp",EDGE,"E38");var subQ3=sQuery(id+"F12.wireOp",EDGE,"E39");Q31=makeQuery(id+"F13.boolean.opBoolean","SPLIT",EDGE,{"disambiguationData":[TD([makeQuery(id+"F5.opExtrude","CAP_FACE",FACE,{"disambiguationData":[OSD([sQuery(id+"F4.wireOp",EDGE,"E18"),subQ0,sQuery(id+"F4.wireOp",EDGE,"E20"),sQuery(id+"F4.wireOp",EDGE,"E21"),sQuery(id+"F4.wireOp",EDGE,"E22"),sQuery(id+"F4.wireOp",EDGE,"E23")])],"isStart":true})])],"derivedFrom":makeQuery(id+"F13.opExtrude","SWEPT_EDGE",EDGE,{"disambiguationData":[OSD([subQ0,subQ2,subQ3])]})});}
            var Q32;
            {var subQ0=sQuery(id+"F12.wireOp",EDGE,"E37");var subQ1=sQuery(id+"F12.wireOp",EDGE,"E38");Q32=makeQuery(id+"F13.boolean.opBoolean","SPLIT",EDGE,{"disambiguationData":[TD([makeQuery(id+"F5.opExtrude","CAP_FACE",FACE,{"disambiguationData":[OSD([sQuery(id+"F4.wireOp",EDGE,"E18"),sQuery(id+"F4.wireOp",EDGE,"E19"),sQuery(id+"F4.wireOp",EDGE,"E20"),sQuery(id+"F4.wireOp",EDGE,"E21"),sQuery(id+"F4.wireOp",EDGE,"E22"),sQuery(id+"F4.wireOp",EDGE,"E23")])],"isStart":true})])],"derivedFrom":makeQuery(id+"F13.opExtrude","SWEPT_EDGE",EDGE,{"disambiguationData":[OSD([subQ0,subQ1])]})});}
            var Q33;
            {var subQ0=sQuery(id+"F0.wireOp",EDGE,"E4");var subQ1=sQuery(id+"F0.wireOp",EDGE,"E3");var subQ3=sQuery(id+"F4.wireOp",EDGE,"E19");Q33=makeQuery(id+"F9.boolean.opBoolean","SPLIT",EDGE,{"disambiguationData":[TD([makeQuery(id+"F5.opExtrude","CAP_FACE",FACE,{"disambiguationData":[OSD([sQuery(id+"F4.wireOp",EDGE,"E18"),subQ3,sQuery(id+"F4.wireOp",EDGE,"E20"),sQuery(id+"F4.wireOp",EDGE,"E21"),sQuery(id+"F4.wireOp",EDGE,"E22"),sQuery(id+"F4.wireOp",EDGE,"E23")])],"isStart":true})])],"derivedFrom":makeQuery(id+"F1.opExtrude","SWEPT_EDGE",EDGE,{"disambiguationData":[OSD([subQ1,subQ0])]})});}
            var Q34;
            {var subQ0=sQuery(id+"F8.wireOp",EDGE,"E25");Q34=makeQuery(id+"F13.boolean.opBoolean","SPLIT",EDGE,{"disambiguationData":[TD([makeQuery(id+"F1.opExtrude","SWEPT_FACE",FACE,{"disambiguationData":[OSD([sQuery(id+"F0.wireOp",EDGE,"E3")])]})])],"derivedFrom":makeQuery(id+"F9.opExtrude","CAP_EDGE",EDGE,{"disambiguationData":[OSD([subQ0])],"isStart":true})});}
            var Q35;
            Q35=makeQuery(id+"F13.boolean.opBoolean","INTERSECT",EDGE,{"derivedFrom":[makeQuery(id+"F9.opExtrude","CAP_FACE",FACE,{"disambiguationData":[OSD([sQuery(id+"F8.wireOp",EDGE,"E24"),sQuery(id+"F8.wireOp",EDGE,"E25"),sQuery(id+"F8.wireOp",EDGE,"E26"),sQuery(id+"F8.wireOp",EDGE,"E27"),sQuery(id+"F8.wireOp",EDGE,"E28"),sQuery(id+"F8.wireOp",EDGE,"E29")])],"isStart":true}),makeQuery(id+"F13.opExtrude","SWEPT_FACE",FACE,{"disambiguationData":[OSD([sQuery(id+"F12.wireOp",EDGE,"E38")])]})]});
            var Q36;
            Q36=makeQuery(id+"F13.opExtrude","CAP_EDGE",EDGE,{"disambiguationData":[OSD([sQuery(id+"F12.wireOp",EDGE,"E38")])],"isStart":true});
            var Q37;
            Q37=makeQuery(id+"F1.opExtrude","CAP_EDGE",EDGE,{"disambiguationData":[OSD([sQuery(id+"F0.wireOp",EDGE,"E1")])],"isStart":true});
            var Q38;
            Q38=makeQuery(id+"F9.opExtrude","CAP_EDGE",EDGE,{"disambiguationData":[OSD([sQuery(id+"F8.wireOp",EDGE,"E26")])],"isStart":false});
            var Q39;
            Q39=makeQuery(id+"F11.boolean.opBoolean","MERGE",EDGE,{"derivedFrom":[makeQuery(id+"F11.opExtrude","CAP_EDGE",EDGE,{"disambiguationData":[OSD([sQuery(id+"F10.wireOp",EDGE,"E32")])],"isStart":false}),makeQuery(id+"F11.opExtrude","CAP_EDGE",EDGE,{"disambiguationData":[OSD([sQuery(id+"F10.wireOp",EDGE,"E35")])],"isStart":false})]});
            var Q40;
            Q40=makeQuery(id+"F9.opExtrude","CAP_EDGE",EDGE,{"disambiguationData":[OSD([sQuery(id+"F8.wireOp",EDGE,"E24")])],"isStart":true});
            var Q41;
            Q41=makeQuery(id+"F11.boolean.opBoolean","MERGE",EDGE,{"derivedFrom":[makeQuery(id+"F11.opExtrude","CAP_EDGE",EDGE,{"disambiguationData":[OSD([sQuery(id+"F10.wireOp",EDGE,"E30")])],"isStart":true}),makeQuery(id+"F11.opExtrude","CAP_EDGE",EDGE,{"disambiguationData":[OSD([sQuery(id+"F10.wireOp",EDGE,"E34")])],"isStart":true})]});
            var Q42;
            Q42=makeQuery(id+"F1.opExtrude","CAP_EDGE",EDGE,{"disambiguationData":[OSD([sQuery(id+"F0.wireOp",EDGE,"E1")])],"isStart":false});
            fillet(context, id + "F14", {"entities" : qUnion([Q0, Q1, Q2, Q3, Q4, Q5, Q6, Q7, Q8, Q9, Q10, Q11, Q12, Q13, Q14, Q15, Q16, Q17, Q18, Q19, Q20, Q21, Q22, Q23, Q24, Q25, Q26, Q27, Q28, Q29, Q30, Q31, Q32, Q33, Q34, Q35, Q36, Q37, Q38, Q39, Q40, Q41, Q42]), "radius" : 1 * mm, "tangentPropagation" : true, "allowEdgeOverflow" : false});
        }
        {
            var Q0;
            Q0=makeQuery(id+"F3.opExtrude","CAP_EDGE",EDGE,{"disambiguationData":[OSD([sQuery(id+"F2.wireOp",EDGE,"E14")])],"isStart":false});
            var Q1;
            Q1=makeQuery(id+"F3.opExtrude","CAP_EDGE",EDGE,{"disambiguationData":[OSD([sQuery(id+"F2.wireOp",EDGE,"E13")])],"isStart":false});
            var Q2;
            Q2=makeQuery(id+"F5.boolean.opBoolean","MERGE",EDGE,{"derivedFrom":[makeQuery(id+"F3.boolean.opBoolean","MERGE",EDGE,{"derivedFrom":[makeQuery(id+"F1.opExtrude","SWEPT_EDGE",EDGE,{"disambiguationData":[OSD([sQuery(id+"F0.wireOp",EDGE,"E4"),sQuery(id+"F0.wireOp",EDGE,"E5")])]}),makeQuery(id+"F3.opExtrude","SWEPT_EDGE",EDGE,{"disambiguationData":[OSD([sQuery(id+"F2.wireOp",EDGE,"E13"),sQuery(id+"F2.wireOp",EDGE,"E14")])]})]}),makeQuery(id+"F5.opExtrude","SWEPT_EDGE",EDGE,{"disambiguationData":[OSD([sQuery(id+"F4.wireOp",EDGE,"E18"),sQuery(id+"F4.wireOp",EDGE,"E19")])]})]});
            var Q3;
            Q3=makeQuery(id+"F5.boolean.opBoolean","MERGE",EDGE,{"derivedFrom":[makeQuery(id+"F3.boolean.opBoolean","MERGE",EDGE,{"derivedFrom":[makeQuery(id+"F1.opExtrude","SWEPT_EDGE",EDGE,{"disambiguationData":[OSD([sQuery(id+"F0.wireOp",EDGE,"E0"),sQuery(id+"F0.wireOp",EDGE,"E7")])]}),makeQuery(id+"F3.opExtrude","SWEPT_EDGE",EDGE,{"disambiguationData":[OSD([sQuery(id+"F2.wireOp",EDGE,"E12"),sQuery(id+"F2.wireOp",EDGE,"E13")])]})]}),makeQuery(id+"F5.opExtrude","SWEPT_EDGE",EDGE,{"disambiguationData":[OSD([sQuery(id+"F4.wireOp",EDGE,"E19"),sQuery(id+"F4.wireOp",EDGE,"E20")])]})]});
            var Q4;
            Q4=makeQuery(id+"F5.opExtrude","CAP_EDGE",EDGE,{"disambiguationData":[OSD([sQuery(id+"F4.wireOp",EDGE,"E18")])],"isStart":false});
            var Q5;
            Q5=makeQuery(id+"F5.opExtrude","CAP_EDGE",EDGE,{"disambiguationData":[OSD([sQuery(id+"F4.wireOp",EDGE,"E19")])],"isStart":false});
            fillet(context, id + "F15", {"entities" : qUnion([Q0, Q1, Q2, Q3, Q4, Q5]), "radius" : 2 * mm, "tangentPropagation" : true, "allowEdgeOverflow" : false});
        }
    });
